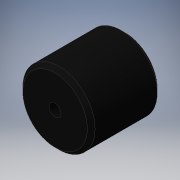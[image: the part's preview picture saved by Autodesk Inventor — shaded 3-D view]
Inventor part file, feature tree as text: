
AUTODESK INVENTOR PART (.ipt)
format: ipt  version: 2016 (Build 200138000, 138)  size: 102,400 bytes
history: native  units: in
note: dims shown in document units (in); Inventor stores cm internally (conversion verified against a paired STEP export)
features: extrude x2, sketch x2, chamfer x1
ambient origin geometry x8: Origin, YZ Plane, XZ Plane, XY Plane, X Axis, Y Axis, Z Axis, Center Point
bodies: Solid1 (feature_tree)
feature tree (5):
  extrude  "Extrusion1"  Depth=0.7087in TaperAngle=0.0deg
  chamfer  "Chamfer1"  Distance=0.0394in Angle=45.0deg
  extrude  "Extrusion2"  Depth=0.7087in TaperAngle=0.0deg
  sketch  "Sketch1"  dims[d0=0.7323in d1=0.7087in d2=0.0in d3=0.0394in d4=0.0787in d5=45.0deg]
  sketch  "Sketch2"  dims[d6=0.122in d7=0.7087in d8=0.0in]
